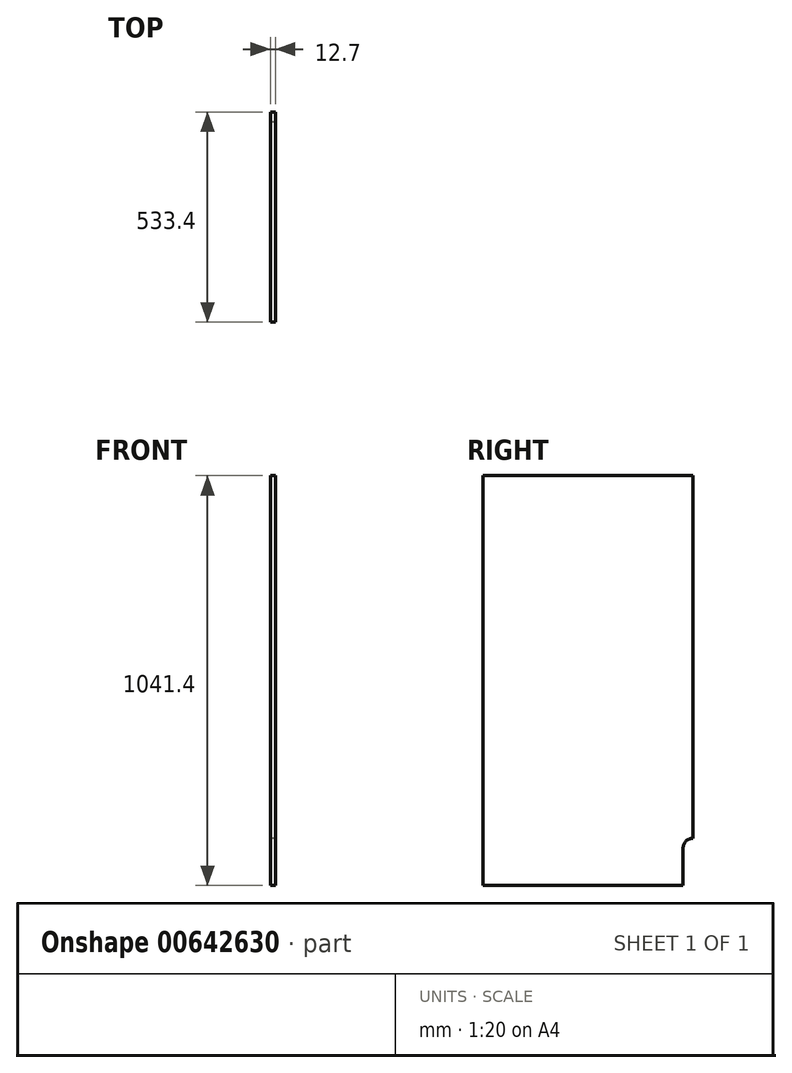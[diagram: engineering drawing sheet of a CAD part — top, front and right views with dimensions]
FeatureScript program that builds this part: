
annotation { "Feature Type Name" : "Feature", "Feature Type Description" : "" }
export const myFeature = defineFeature(function(context is Context, id is Id, definition is map)
    precondition{}
    {
        {
            var Q0;
            Q0=qCreatedBy(makeId("Right.planeOp"),FACE);
            var sketch = newSketch(context, id + "F0", { "sketchPlane" : qUnion([Q0])});
            skLineSegment(sketch, "E0.bottom", {"start": v(0, 520.7) * mm, "end": v(-533.4, 520.7) * mm});
            skLineSegment(sketch, "E0.top", {"start": v(-25.4, -520.7) * mm, "end": v(-533.4, -520.7) * mm});
            skLineSegment(sketch, "E0.left", {"start": v(0, 520.7) * mm, "end": v(0, -400.7) * mm});
            skLineSegment(sketch, "E0.right", {"start": v(-533.4, 520.7) * mm, "end": v(-533.4, -520.7) * mm});
            skPoint(sketch, "E0.middle", {"position": v(-266.7, 0) * mm});
            skLineSegment(sketch, "E1", {"start": v(-25.4, -426.1) * mm, "end": v(-25.4, -520.7) * mm});
            skArc(sketch, "E2", {"start": v(-25.4, -426.1) * mm, "mid": v(-17.96, -408.14) * mm, "end": v(0, -400.7) * mm});
            skPoint(sketch, "E3.orphan", {"position": v(0, -520.7) * mm});
            skSolve(sketch);
        }
        {
            var Q0;
            Q0=makeQuery(id+"F0.imprint","IMPRINT",FACE,{"disambiguationData":[TD([[makeQuery(id+"F0.imprint","IMPRINT",EDGE,{"derivedFrom":sQuery(id+"F0.wireOp",EDGE,"E0.bottom")}),1.0]])]});
            extrude(context, id + "F1", {"entities" : qUnion([Q0]), "depth" : 12.7 * mm, "offsetDistance" : 25 * mm});
        }
    });
